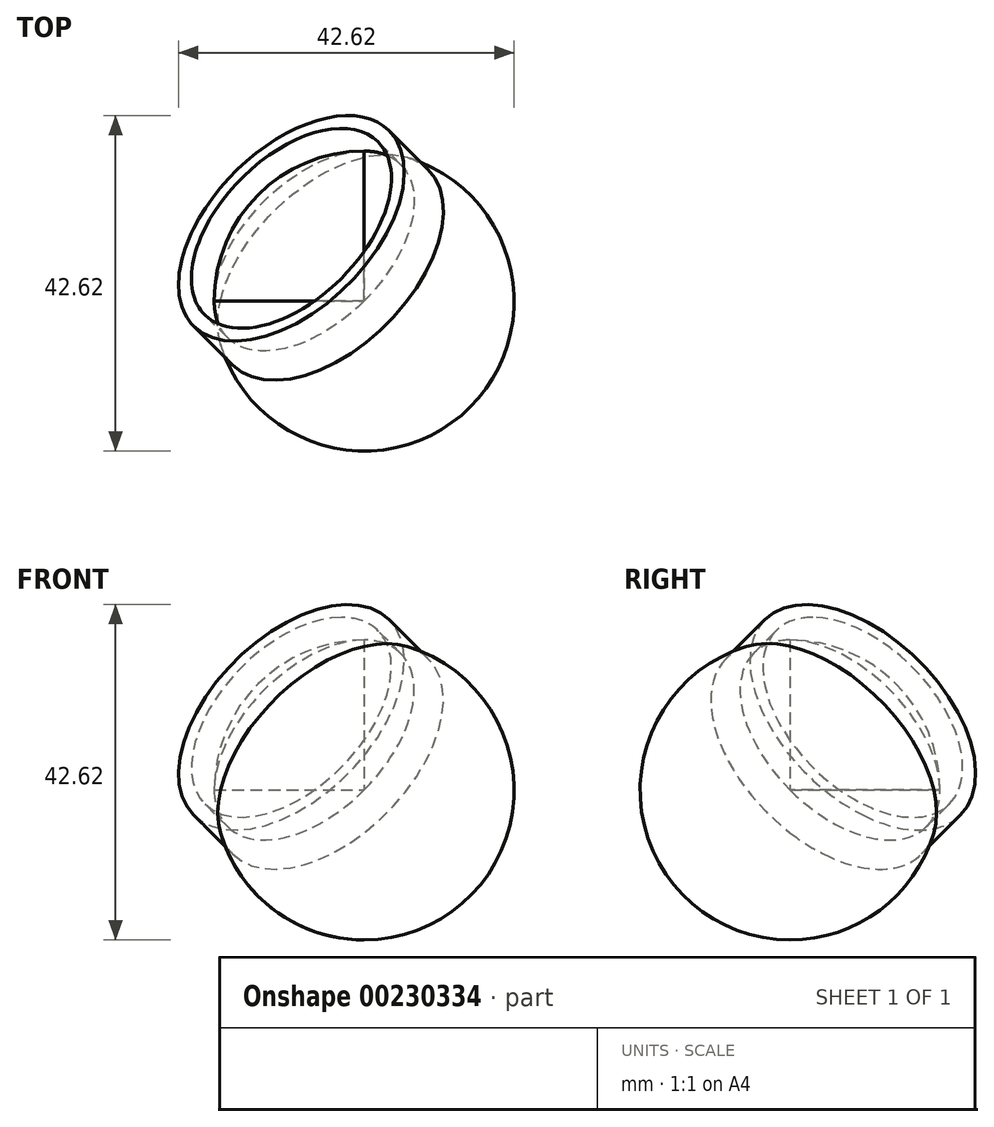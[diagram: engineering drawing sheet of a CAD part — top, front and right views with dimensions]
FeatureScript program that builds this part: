
annotation { "Feature Type Name" : "Feature", "Feature Type Description" : "" }
export const myFeature = defineFeature(function(context is Context, id is Id, definition is map)
    precondition{}
    {
        {
            var Q0;
            Q0=qCreatedBy(makeId("Front.planeOp"),FACE);
            var sketch = newSketch(context, id + "F0", { "sketchPlane" : qUnion([Q0])});
            skLineSegment(sketch, "E0", {"start": v(0, 19.05) * mm, "end": v(0, -19.05) * mm});
            skArc(sketch, "E1", {"start": v(0, 19.05) * mm, "mid": v(-19.05, 0) * mm, "end": v(0, -19.05) * mm});
            skSolve(sketch);
        }
        {
            var Q0;
            Q0=makeQuery(id+"F0.imprint","IMPRINT",FACE,{"disambiguationData":[TD([[makeQuery(id+"F0.imprint","IMPRINT",EDGE,{"derivedFrom":sQuery(id+"F0.wireOp",EDGE,"E0")}),-1.0]])]});
            var Q1;
            Q1=sQuery(id+"F0.wireOp",EDGE,"E0");
            revolve(context, id + "F1", {"entities" : qUnion([Q0]), "axis" : qUnion([Q1]), "revolveType" : RevolveType.FULL});
        }
        {
            var Q0;
            Q0=qCreatedBy(makeId("Front.planeOp"),FACE);
            var sketch = newSketch(context, id + "F2", { "sketchPlane" : qUnion([Q0])});
            skArc(sketch, "E2", {"start": v(0, 19.05) * mm, "mid": v(-13.47, 13.47) * mm, "end": v(-19.05, 0) * mm});
            skLineSegment(sketch, "E3", {"start": v(-19.05, 0) * mm, "end": v(0, 0) * mm});
            skLineSegment(sketch, "E4", {"start": v(0, 19.05) * mm, "end": v(0, 0) * mm});
            skSolve(sketch);
        }
        {
            var Q0;
            Q0=qSketchRegion(id+"F2",true);
            extrude(context, id + "F3", {"entities" : qUnion([Q0]), "operationType" : NewBodyOperationType.REMOVE, "oppositeDirection" : true, "depth" : 25 * mm});
        }
        {
            var Q0;
            Q0=makeQuery(id+"F3.boolean.opBoolean","COPY",VERTEX,{"derivedFrom":makeQuery(id+"F3.opExtrude","CAP_VERTEX",VERTEX,{"disambiguationData":[OSD([sQuery(id+"F2.wireOp",EDGE,"E2"),sQuery(id+"F2.wireOp",EDGE,"E4")])],"isStart":true})});
            var Q1;
            Q1=makeQuery(id+"F3.boolean.opBoolean","INTERSECT",VERTEX,{"derivedFrom":[makeQuery(id+"F1.opRevolve","SWEPT_FACE",FACE,{"disambiguationData":[OSD([sQuery(id+"F0.wireOp",EDGE,"E1")])]}),makeQuery(id+"F3.opExtrude","SWEPT_FACE",FACE,{"disambiguationData":[OSD([sQuery(id+"F2.wireOp",EDGE,"E3")])]}),makeQuery(id+"F3.opExtrude","SWEPT_FACE",FACE,{"disambiguationData":[OSD([sQuery(id+"F2.wireOp",EDGE,"E4")])]})]});
            var Q2;
            Q2=makeQuery(id+"F3.boolean.opBoolean","COPY",VERTEX,{"derivedFrom":makeQuery(id+"F3.opExtrude","CAP_VERTEX",VERTEX,{"disambiguationData":[OSD([sQuery(id+"F2.wireOp",EDGE,"E2"),sQuery(id+"F2.wireOp",EDGE,"E3")])],"isStart":true})});
            cPlane(context, id + "F4", {"entities" : qUnion([Q0, Q1, Q2]), "cplaneType" : CPlaneType.THREE_POINT, "offset" : 25 * mm, "width" : 150 * mm, "height" : 150 * mm});
        }
        {
            var Q0;
            Q0=qCreatedBy(id+"F4.planeOp",FACE);
            var sketch = newSketch(context, id + "F5", { "sketchPlane" : qUnion([Q0])});
            skCircle(sketch, "E5", {"center": v(0, 0) * mm, "radius": 15.55 * mm});
            skCircle(sketch, "E6.0", {"center": v(0, 0) * mm, "radius": 17.55 * mm});
            skSolve(sketch);
        }
        {
            var Q0;
            Q0=makeQuery(id+"F5.imprint","IMPRINT",FACE,{"disambiguationData":[TD([[makeQuery(id+"F5.imprint","IMPRINT",EDGE,{"derivedFrom":sQuery(id+"F5.wireOp",EDGE,"E5")}),-1.0]])]});
            var Q1;
            Q1=makeQuery(id+"F1.opRevolve","SWEPT_FACE",FACE,{"disambiguationData":[OSD([sQuery(id+"F0.wireOp",EDGE,"E1")])]});
            extrude(context, id + "F6", {"entities" : qUnion([Q0]), "operationType" : NewBodyOperationType.ADD, "endBound" : BoundingType.UP_TO_SURFACE, "endBoundEntityFace" : qUnion([Q1]), "depth" : 25 * mm, "hasSecondDirection" : true, "secondDirectionOppositeDirection" : true, "secondDirectionDepth" : 5 * mm});
        }
        {
            var Q0;
            Q0=qCreatedBy(id+"F4.planeOp",FACE);
            var sketch = newSketch(context, id + "F7", { "sketchPlane" : qUnion([Q0])});
            skLineSegment(sketch, "E7", {"start": v(18.8, 0) * mm, "end": v(-19.12, 0) * mm});
            skSolve(sketch);
        }
    });
